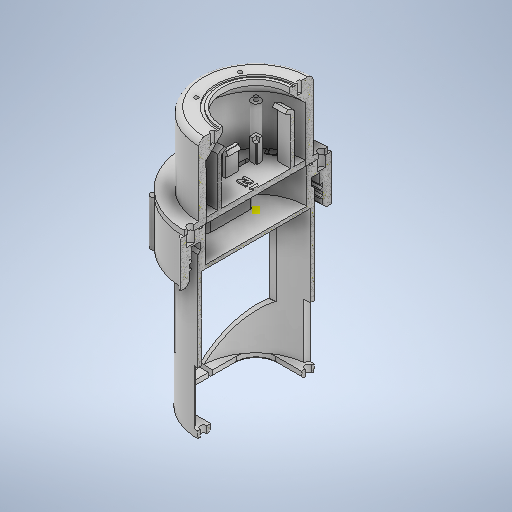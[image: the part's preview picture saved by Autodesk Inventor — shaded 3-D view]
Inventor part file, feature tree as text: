
AUTODESK INVENTOR PART (.ipt)
format: ipt  version: 2025.2 (Build 292293000, 293)  size: 2,590,720 bytes
history: native  units: in
note: dims shown in document units (in); Inventor stores cm internally (conversion verified against a paired STEP export)
features: extrude x57, projected_geometry x19, sketch x16, mirror x9, other x8, fillet x7, chamfer x7, pattern_circular x3, plane x3, helix x1
ambient origin geometry x8: Origin, YZ Plane, XZ Plane, XY Plane, X Axis, Y Axis, Z Axis, Center Point
bodies: Body1 (feature_tree), Body2 (feature_tree), Body3 (feature_tree), Body4 (feature_tree), Body5 (feature_tree), Body6 (feature_tree)
feature tree (130):
  other  "BatteryCage"
  sketch  "Sketch1"  dims[d0=2.5748in d1=0.0098in]
  extrude  "Start of Battery Cage"  Depth=0.0098in
  extrude  "Extrusion2"  Depth=0.4724in
  extrude  "Extrusion3"  Depth=0.0984in
  fillet  "Fillet1"  Radius=0.1969in
  chamfer  "Chamfer1"  Distance=0.0984in
  fillet  "Fillet2"  Radius=0.1181in
  extrude  "Extrusion4"  Depth=0.0197in
  chamfer  "Chamfer2"  Distance=0.0787in Angle=45.0deg
  sketch  "Sketch4"  dims[d2=2.0512in d3=0.4724in]
  extrude  "Extrusion6"  Depth=4.4724in TaperAngle=0.0deg
  mirror  "Mirror1"
  extrude  "Battery Eject Hole"  Depth=0.0787in
  extrude  "Start of Pi Cage"  Depth=0.5906in TaperAngle=0.0deg
  extrude  "Extrusion9"  Depth=0.0512in
  chamfer  "Chamfer4"  Distance=0.0984in
  extrude  "Extrusion10"  Depth=0.0787in TaperAngle=45.0deg
  extrude  "Shave Down for 40oz"  Depth=0.0984in
  fillet  "Battery Bottom Fillet"  Radius=2.0472in
  extrude  "Extrusion11"  Depth=0.0394in
  extrude  "Extrusion12"  Depth=0.0394in TaperAngle=0.0deg
  extrude  "Extrusion13"  Depth=0.0394in TaperAngle=0.0deg
  extrude  "Extrusion14"  Depth=0.0394in
  chamfer  "Chamfer5"  [1 undecoded]
  extrude  "Extrusion15"  Depth=0.0394in
  extrude  "Extrusion17"  Depth=0.0787in
  extrude  "Extrusion18"  Depth=0.0394in
  extrude  "Extrusion19"  Depth=0.0984in
  pattern_circular  "Circular Pattern1"  [2 undecoded]
  extrude  "Extrusion20"  Depth=0.0394in
  pattern_circular  "Circular Pattern2"  [2 undecoded]
  helix  "Coil1"  [1 undecoded]
  extrude  "Extrusion21"  Depth=0.0394in TaperAngle=0.0deg
  extrude  "Extrusion22"  Depth=0.0787in TaperAngle=45.0deg
  extrude  "Extrusion23"  Depth=0.0394in TaperAngle=0.0deg
  extrude  "Extrusion24"  Depth=0.0394in
  chamfer  "Chamfer6"  Distance=0.5906in
  extrude  "Tower O-ring Gland"  Depth=0.0394in
  extrude  "Sensor Tower Base"  TaperAngle=0.0deg  [1 undecoded]
  extrude  "Extrusion27"  Depth=0.0394in
  extrude  "Extrusion28"  Depth=0.0394in
  extrude  "Extrusion34"  Depth=0.0394in
  extrude  "Extrusion35"  TaperAngle=0.0deg  [1 undecoded]
  extrude  "Extrusion36"  Depth=0.0394in
  extrude  "North Indicator"  TaperAngle=0.0deg  [1 undecoded]
  extrude  "Extrusion37"  Depth=0.0394in
  extrude  "Extrusion38"  Depth=0.0394in
  mirror  "Mirror2"
  extrude  "Extrusion39"  Depth=0.0394in TaperAngle=0.0deg
  extrude  "Extrusion40"  Depth=0.0394in TaperAngle=360.0deg
  extrude  "Extrusion41"  Depth=0.1575in
  mirror  "Mirror3"
  extrude  "Extrusion56"  Depth=0.0394in TaperAngle=0.0deg
  mirror  "Mirror8"
  extrude  "Magnetometer Retaining Tab"  Depth=0.0394in TaperAngle=360.0deg
  extrude  "Retaining Tap Ramp"  Depth=0.0394in
  mirror  "Mirror Retaining Tab"
  extrude  "Start of Cover"  Depth=0.0394in
  extrude  "Extrusion30"  Depth=0.0394in
  sketch  "Sketch47"  dims[d37=0.0in]
  extrude  "Extrusion52"  Depth=0.0787in
  plane  "Work Plane4"
  extrude  "Extrusion53"  Depth=0.0394in
  mirror  "Mirror4"
  mirror  "Mirror5"
  fillet  "Fillet7"  Radius=0.1457in
  extrude  "Extrusion50"  Depth=0.3937in
  extrude  "Trim Pi Cage for 40oz"  Depth=0.3937in TaperAngle=0.0deg
  extrude  "Extrusion31"  Depth=0.0394in
  chamfer  "Chamfer7"  [1 undecoded]
  extrude  "Extrusion32"  Depth=0.3937in TaperAngle=0.0deg
  pattern_circular  "Circular Pattern3"  [2 undecoded]
  extrude  "Dome O-ring Gland"  Depth=0.0394in
  fillet  "Fillet4"  Radius=0.3937in
  plane  "Work Plane2"
  extrude  "Extrusion47"  Depth=0.0787in TaperAngle=45.0deg
  extrude  "Indexing tab"  Depth=0.0394in
  mirror  "Mirror6"
  chamfer  "Chamfer8"  [1 undecoded]
  extrude  "Manufacturability: Sensor Cover Base"  Depth=0.0394in
  extrude  "North Marker External"  Depth=0.0394in
  extrude  "Start of Camera"  Depth=0.0394in
  fillet  "Fillet5"  [1 undecoded]
  extrude  "Extrusion43"  Depth=0.0394in
  plane  "Work Plane1"
  extrude  "Extrusion45"  Depth=0.0394in
  extrude  "Extrusion46"  Depth=0.0394in
  fillet  "Fillet6"  Radius=0.1969in
  mirror  "Mirror7"
  other  "Start of Dome"
  extrude  "Extrusion61"  Depth=0.0394in
  projected_geometry  "Projected Loop1"
  projected_geometry  "Projected Loop2"
  other  "StartOfPiCage"
  other  "PiCage"
  projected_geometry  "Projected Loop3"
  sketch  "Sketch10"  dims[d4=0.0984in d5=0.0in d6=0.0079in d7=0.1969in]
  projected_geometry  "Projected Loop4"
  sketch  "Sketch17"  dims[d8=0.7874in]
  projected_geometry  "Projected Loop5"
  other  "SensorTower"
  other  "SensorCover"
  sketch  "Sketch33"  dims[d9=0.1969in d10=0.0984in d11=0.0in d12=0.1181in]
  projected_geometry  "Projected Loop7"
  projected_geometry  "Projected Loop8"
  projected_geometry  "Projected Loop9"
  projected_geometry  "Projected Loop10"
  projected_geometry  "Projected Loop11"
  sketch  "Sketch35"  dims[d13=0.3937in d14=0.0in d15=0.0197in d16=0.0512in d17=0.0787in d18=45.0deg]
  projected_geometry  "Projected Loop12"
  other  "Camera"
  sketch  "Sketch39"  dims[d19=0.1181in d20=4.4724in d21=0.0in]
  sketch  "Sketch40"  dims[d22=0.0512in d23=0.0787in d24=45.0deg d25=0.0512in]
  sketch  "Sketch43"  dims[d31=0.1732in d32=0.5906in d33=0.0in]
  sketch  "Sketch44"  dims[d34=0.0512in d35=0.0512in]
  sketch  "Sketch45"  dims[d36=0.0512in]
  projected_geometry  "Projected Loop13"
  projected_geometry  "Projected Loop14"
  projected_geometry  "Projected Loop15"
  sketch  "Sketch52"  dims[d38=0.0512in]
  projected_geometry  "Projected Loop16"
  other  "Clear Dome"
  projected_geometry  "Projected Loop17"
  sketch  "Sketch54"  dims[d41=0.1476in d42=0.0984in d43=0.0in]
  projected_geometry  "Projected Loop18"
  projected_geometry  "Projected Loop19"
  sketch  "Sketch56"  dims[d44=0.0512in d45=0.0787in d46=45.0deg]
  sketch  "Sketch57"  dims[d47=0.0984in d48=0.0984in d49=2.0472in d50=0.2756in d51=2.9528in d52=0.0in d53=1.1811in d54=0.0in d55=0.5669in d56=0.0in d57=0.8661in d58=0.0787in d59=0.6299in d60=0.0984in d61=0.0in d62=0.1772in d63=0.2756in d64=0.0172in d65=0.9843in d66=0.0in d67=0.9843in d68=0.0787in d69=45.0deg d70=0.1969in d71=0.0in d72=0.7874in d73=0.5906in d74=0.5669in d75=0.0in d76=3.1181in d77=0.1122in d78=0.2756in d79=0.0in d80=0.7087in d81=0.0in d82=0.1732in d83=1.4173in d84=0.2362in d85=0.0in d86=1.5748in d87=360.0deg d89=0.1575in d90=0.2756in d91=0.0in d92=3.1496in d93=360.0deg d95=2.4016in d96=0.185in d97=0.1102in d98=0.0787in d99=1.4016in d100=0.1457in d101=0.3937in d102=0.9449in d103=0.0in d104=90.0deg d105=90.0deg d106=0.0in d107=0.0in d108=0.3937in d109=0.0in d110=0.2362in d111=0.0in d112=0.3937in d113=0.0in d114=0.2756in d115=0.2756in d116=0.3937in d117=0.0in d118=0.0768in d119=0.0787in d120=45.0deg d127=0.1181in d128=0.0in d129=2.126in d130=0.2953in d131=1.4173in d132=0.0in d133=1.4961in d134=1.3386in d135=0.0709in d136=0.1969in d137=0.9843in d138=0.0in d139=0.2756in d141=2.1654in d142=0.1575in d144=0.1181in d145=0.0in d146=0.1575in d147=1.4173in d148=0.0in d149=1.4567in d150=0.1181in d151=0.0in d152=0.3543in d153=0.0787in d154=45.0deg d155=0.9449in d156=0.0866in d157=0.2362in d158=0.0in d159=2.3622in d160=360.0deg d162=1.5748in d163=0.0669in d164=0.0354in d165=0.0in d167=0.1181in d168=0.0787in d169=0.0787in d170=45.0deg d171=1.0079in d172=1.0in d173=0.0197in d174=0.0591in d175=0.0591in d176=0.3937in d177=0.0in d178=0.4724in d179=0.0in d180=0.0787in d181=0.0787in d182=0.4724in d183=0.0in d184=0.2756in d185=0.5118in d186=0.0in d187=45.0deg d188=0.0591in d189=0.5512in d190=0.0in d191=0.0472in d192=30.0deg d193=0.0315in d194=0.0787in d195=0.0787in d196=0.0in d197=0.5512in d198=1.2008in d199=0.0in d200=0.063in d201=45.0deg d202=30.0deg d203=0.1181in d204=0.0945in d205=1.2008in d206=0.0in d207=1.4961in d208=0.0984in d209=0.063in d210=0.0in d211=0.0394in d212=1.1772in d213=0.689in d214=0.0in d215=0.0276in d216=0.0in d217=0.0787in d218=0.1378in d219=0.3937in d220=0.126in d221=0.0in d222=0.7835in d223=0.3937in d224=0.0in d225=0.3858in d229=-0.0236in d230=0.1772in d231=0.748in d232=0.3937in d233=0.0in d234=0.0197in d235=0.3937in d236=0.0in d237=0.1024in d238=0.0197in d239=0.0197in d240=0.3937in d241=0.0in d242=2.126in d243=0.1476in d244=2.1654in d245=0.1181in d246=0.0in d247=30.0deg d248=0.1575in d251=0.3937in d252=0.0in d253=45.0deg d254=0.1181in d255=0.1575in d256=0.0in d257=0.0394in d258=0.1378in d259=0.0in d260=2.4409in d261=2.3228in d262=0.0354in d263=0.0in d264=0.0787in d265=0.0787in d266=1.063in d267=0.3031in d268=1.6299in d269=0.0787in d270=360.0deg d271=0.0098in d272=0.0in d274=0.3782in d275=0.1683in d276=0.0787in d277=0.2756in d278=0.1378in d279=0.5118in d280=0.0in d281=0.0591in d282=0.0472in d283=30.0deg d284=45.0deg d285=0.0315in d286=0.5118in d287=0.0in d288=0.1458in d289=0.1378in d290=0.1181in d291=0.0in d292=0.2953in d293=0.2756in d294=0.0591in d295=0.0in d296=0.0394in d298=0.0394in d300=0.0591in d301=0.7638in d302=0.0in]
  projected_geometry  "Projected Loop20"
note: 14 required parameter values undecoded (feature->parameter linkage not recoverable at this tier; creation-order binding heuristic only, values carry confidence <= 0.55)
